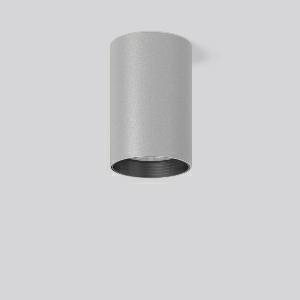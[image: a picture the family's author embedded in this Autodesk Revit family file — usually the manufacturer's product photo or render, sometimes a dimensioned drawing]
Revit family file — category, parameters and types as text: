
# Revit family: heledon_maxi_a_931236_004_3e92
name_source: partatom
category: Lighting Fixtures
units: mm (PartAtom-declared; Revit-internal decimal feet)

## family parameters
Cut with Voids When Loaded = No
Host = Face
Light Source = No
Part Type = Normal
Room Calculation Point = No
Round Connector Dimension = Use Diameter
Shared = No

## types (1)
- HELEDON maxi A (1 x LED Modul 932 fresh meat, 1800 lm, 3200)
    Apparent Load = 33 VA
    Approval mark = CE
    CIE Flux Codes = 96 99 100 100 100
    Color Rendering = 90
    Color Temperature = 3200
    Default Elevation = 1800 mm  [stored 5.90551 ft]
    Description = Series: HELEDON maxi
Cylindrical surface-mounted downlight. Housing: die-cast aluminium, powder-coated. Internal ceiling frame polycarbonate with bayonet mounting. Black plastic ring and recessed LED to prevent glare from the side. Optical assembly with lens made of plastic (polycarbonate) for the best homogeneous light distribution - can be changed without tools. Special LED for illumination of meat included. Suitable for Ceiling mounting. Easy installation with a separate ceiling frame with bayonet mounting and plug connection. Driver integrated. Connected via plug-in connector. High quality converter without flickering and stroboscopic effect. The following accessories can be mounted without use of tools: interchangeable lenses, decorative glasses, honeycomb louvre, clear and frosted diffusers, white interchangeable plastic ring. 
Colour: silver
Diameter: 123 mm
Height: 183 mm
Lamp: LED
Socket: without socket
Colour temperature: fresh meat
System power: 33 W
Rated luminous flux: 1800 lm
Luminous efficiency: 55 lm/W
Control gear: Regulated power supply
Protection class: I
Type of protection: IP 20
    Height = 183 mm
    Lamp = 1 x LED Modul 932 fresh meat
    Lamp Light Flux = 1800 lm
    Lamp count = 1
    Length = 123 mm
    Lifetime = 50000 h
    Luminous efficacy = 55 lm/W
    Manufacturer = RZB
    ModVariant = No
    Model = 931236.004
    Mounting Place = Ceiling
    Mounting Type = Surface mounted
    Number of Poles = 1
    OnlyDefault = Yes
    Power Factor = 1
    Product Name = HELEDON maxi A
    Product group = Surface mounted downlights
    ProductGroupID = 302
    Protection Class = Protection class I
    Protection Degree = IP 20
    RLX_Detail_Level = 1
    RLX_Emergency_Light_Flux = 0 lm
    RLX_Emergency_Type = 0
    RLX_Emergency_Type_DB = No
    RlxData = <blob elided: 97913 chars, md5=b2256876>
    Socket = socket
    Standby Power = 0 W
    System Light Flux = 1800 lm
    System Power = 33 W
    Type Comments = Product without accessories
    Type Image = 931193.004.jpg
    URL = http://relux.com
    VarID = ---
    Voltage = 230 V
    Voltage Range = 220-240 V
    Weight = 0.00 kg
    Width = 0 mm  [stored 0 ft]

note: [stored X ft] marks values corroborated as IEEE doubles in the binary element streams (Revit-internal decimal feet)

## geometry (parser evidence)
native form markers: Blend x4, Sweep x9
no freeform markers — native parametric forms only
